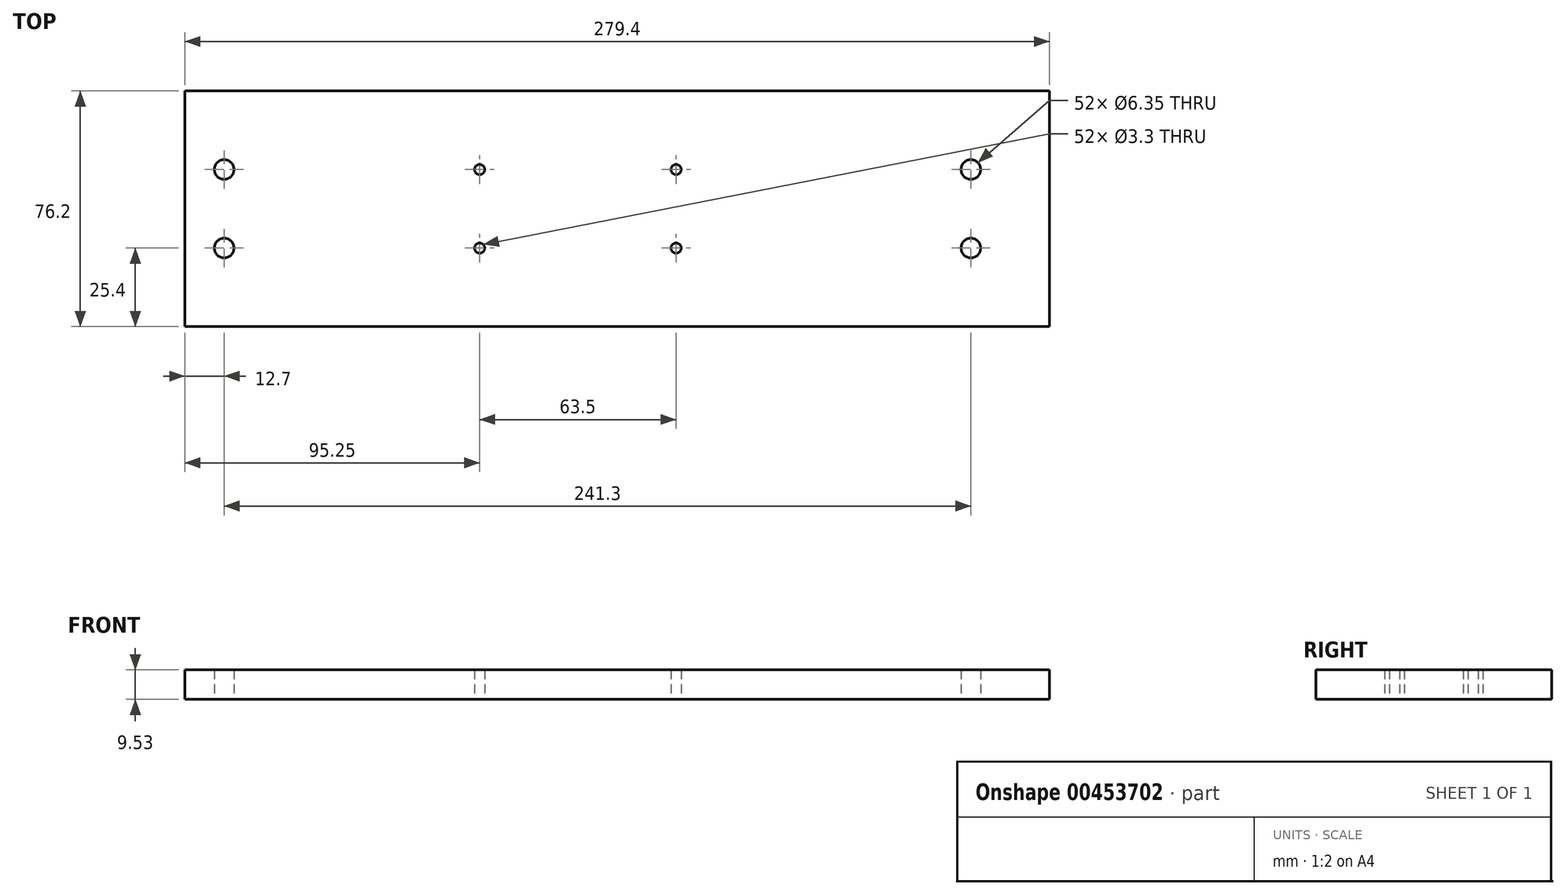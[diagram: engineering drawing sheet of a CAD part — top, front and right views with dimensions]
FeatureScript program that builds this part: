
annotation { "Feature Type Name" : "Feature", "Feature Type Description" : "" }
export const myFeature = defineFeature(function(context is Context, id is Id, definition is map)
    precondition{}
    {
        {
            var Q0;
            Q0=qCreatedBy(makeId("Top.planeOp"),FACE);
            var sketch = newSketch(context, id + "F0", { "sketchPlane" : qUnion([Q0])});
            skLineSegment(sketch, "E0.bottom", {"start": v(-139.7, 38.1) * mm, "end": v(139.7, 38.1) * mm});
            skLineSegment(sketch, "E0.top", {"start": v(-139.7, -38.1) * mm, "end": v(139.7, -38.1) * mm});
            skLineSegment(sketch, "E0.left", {"start": v(-139.7, 38.1) * mm, "end": v(-139.7, -38.1) * mm});
            skLineSegment(sketch, "E0.right", {"start": v(139.7, 38.1) * mm, "end": v(139.7, -38.1) * mm});
            skCircle(sketch, "E1", {"center": v(-127, 12.7) * mm, "radius": 3.17 * mm});
            skCircle(sketch, "E2", {"center": v(-127, -12.7) * mm, "radius": 3.18 * mm});
            skCircle(sketch, "E3", {"center": v(-44.45, 12.7) * mm, "radius": 1.65 * mm});
            skCircle(sketch, "E4", {"center": v(-44.45, -12.7) * mm, "radius": 1.65 * mm});
            skCircle(sketch, "E5", {"center": v(19.05, 12.7) * mm, "radius": 1.65 * mm});
            skCircle(sketch, "E6", {"center": v(19.05, -12.7) * mm, "radius": 1.65 * mm});
            skCircle(sketch, "E7", {"center": v(114.3, 12.7) * mm, "radius": 3.18 * mm});
            skCircle(sketch, "E8", {"center": v(114.3, -12.7) * mm, "radius": 3.18 * mm});
            skSolve(sketch);
        }
        {
            var Q0;
            Q0=makeQuery(id+"F0.imprint","IMPRINT",FACE,{"disambiguationData":[TD([[makeQuery(id+"F0.imprint","IMPRINT",EDGE,{"derivedFrom":sQuery(id+"F0.wireOp",EDGE,"E0.bottom")}),-1.0]])]});
            extrude(context, id + "F1", {"entities" : qUnion([Q0]), "depth" : 9.52 * mm});
        }
    });
